# Revit family: Geberit Sigma concealed cistern 8 cm, 4.5 _ 3 litres_PRO_219125
name_source: partatom
category: Plumbing Fixtures
units: mm (PartAtom-declared; Revit-internal decimal feet)

## family parameters
Always vertical = Yes
Cut with Voids When Loaded = No
OmniClass Number = 23.31.19.00
Part Type = Normal
Room Calculation Point = Yes
Round Connector Dimension = Use Diameter
Shared = No
Work Plane-Based = No

## types (1)
- 109.795.00.1 Geberit Sigma concealed cistern 8 cm, 4.5 / 3 litres
    B = 410 mm  [stored 1.34514 ft]
    CW Connection = Yes
    D1 = 50 mm  [stored 0.164042 ft]
    Default Elevation = 0 mm  [stored 0 ft]
    Description = Geberit Sigma concealed cistern 8 cm, 4.5 / 3 litres
    EAN code basic data = 4025416543893
    Flow pressure = 0.1-10 bar
    Flush volume large, adjustment range = 4.5 / 6 / 7.5 l
    Flush volume small, adjustment range = 3-4 l
    Flush volume, factory setting = 4.5 and 3 l
    GEB_culture = en-AU
    GEB_generic_description = concealed cistern for toilet
    GEB_generic_manufacturer = generic
    GEB_imperial_engineering = No
    GEB_metric_engineering = Yes
    GEB_pimversion = 23.08.14
    GEB_processing_type = T
    GEB_reference = PRO_219125
    GEB_translations = {"ATT_10673":"EAN code basic data","ATT_10773":"Flow pressure","ATT_10807":"Flush volume large, adjustment range","ATT_10811":"Flush volume small, adjustment range","ATT_10832":"Maximum operating temperature, water","ATT_10866":"Flush volume, factory setting","ATT_10931":"B","ATT_10951":"H","ATT_380239":"T"}
    GEB_use_DN = Yes
    H = 625 mm  [stored 2.05052 ft]
    HW Connection = No
    IfcDescription = Geberit Sigma concealed cistern 8 cm, 4.5 / 3 litres
    IfcExportAs = IfcSanitaryTerminal
    IfcExportType = CISTERN
    LOD300 = No
    LOD400 = Yes
    Manufacturer = Geberit
    Maximum operating temperature, water = 25 °C
    Model = Sigma 8 cm
    T = 80 mm  [stored 0.262467 ft]
    Vent Connection = No
    Waste Connection = Yes
    applicationPurposes = For drywall construction
For installation in part or room-height prewall installations
For installation in room-height installation walls
For floor-standing WCs
For single flush, dual flush or stop-and-go flush
    application_range = sanitary systems
    brandName = Geberit
    characteristics = Range 2016
Concealed cistern with front actuation
Concealed cistern, fully insulated against condensation
Cistern fulfils standard requirements in accordance with AS 1172.2:2004
Immediate post flush possible with factory setting
Flush bend fitted
Tool-free installation and maintenance work on concealed cistern
Water supply connection on the top left
Water supply connection, dezincification-resistant
Protection cover box for service opening protects against moisture and dirt
Protection box for service opening can be cut to length, suitable for surface-even actuator plates
    cistern_bottom = 625 mm  [stored 2.05052 ft]
    cistern_depth = 80 mm  [stored 0.262467 ft]
    cistern_top_offset = 0 mm  [stored 0 ft]
    cistern_width = 410 mm  [stored 1.34514 ft]
    connection_bend = No
    connection_description1 = cold water in
    connection_description2 = sanitary out
    content_date_changed = 2023.07.05
    content_version = GEB MG 1.6
    fixed_material = Geberit, Plastic, Opaque white
    fixed_material_01 = Geberit, Laminate, Ivory, Matte
    fixed_material_03 = Geberit, PE-HD, Black
    flushing_water_pipe_D = 80 mm  [stored 0.262467 ft]
    key 1000 = 109.795.00.1
    name = Geberit Sigma concealed cistern 8 cm, 4.5 / 3 litres
    outlet_flow = 0.0 L/s
    scopeOfDelivery = Water supply connection Rp 1/2" - R 1/2", compatible with MF, with integrated angle stop valve and hand wheel
Protection box for service opening
Flush bend 90°
Flush bend extension, ø 45 mm
Fastening for flush bend
2 sleeves made of EPDM
Protection plug
Fastening material for drywall
    type = Sigma 8 cm

note: [stored X ft] marks values corroborated as IEEE doubles in the binary element streams (Revit-internal decimal feet)

## geometry (parser evidence)
native form markers: Blend x4, Sweep x6
no freeform markers — native parametric forms only
